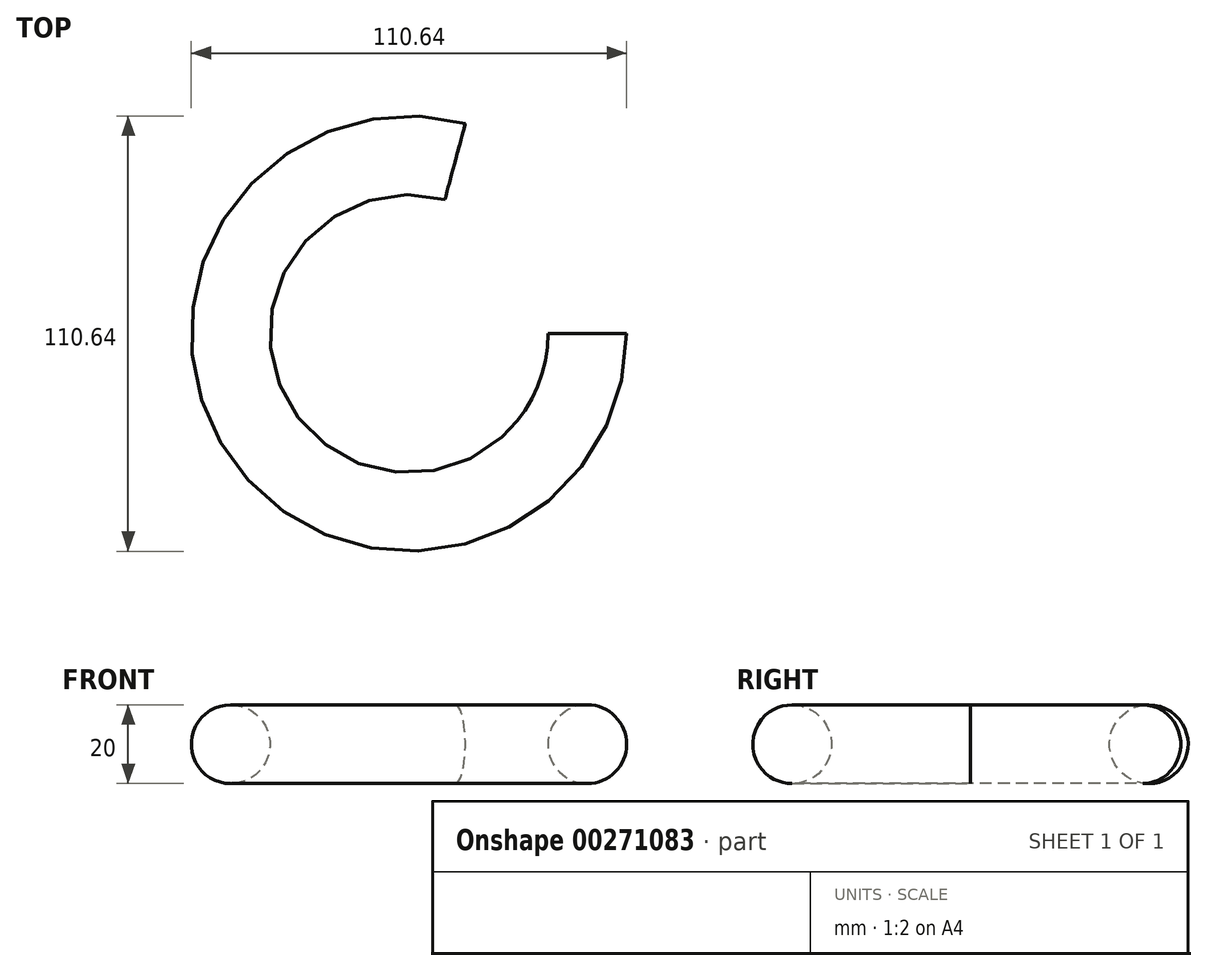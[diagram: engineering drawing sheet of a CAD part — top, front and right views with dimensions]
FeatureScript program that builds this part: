
annotation { "Feature Type Name" : "Feature", "Feature Type Description" : "" }
export const myFeature = defineFeature(function(context is Context, id is Id, definition is map)
    precondition{}
    {
        {
            var Q0;
            Q0=qCreatedBy(makeId("Front.planeOp"),FACE);
            var sketch = newSketch(context, id + "F0", { "sketchPlane" : qUnion([Q0])});
            skCircle(sketch, "E0", {"center": v(45.32, 0) * mm, "radius": 10 * mm});
            skLineSegment(sketch, "E1", {"start": v(0, 29.29) * mm, "end": v(0, -32.6) * mm, "construction": true});
            skSolve(sketch);
        }
        {
            var Q0;
            Q0=makeQuery(id+"F0.imprint","IMPRINT",FACE,{"disambiguationData":[TD([[makeQuery(id+"F0.imprint","IMPRINT",EDGE,{"derivedFrom":sQuery(id+"F0.wireOp",EDGE,"E0")}),1.0]])]});
            var Q1;
            Q1=sQuery(id+"F0.wireOp",EDGE,"E1");
            revolve(context, id + "F1", {"entities" : qUnion([Q0]), "axis" : qUnion([Q1]), "revolveType" : RevolveType.ONE_DIRECTION, "angle" : 285 * degree});
        }
    });
